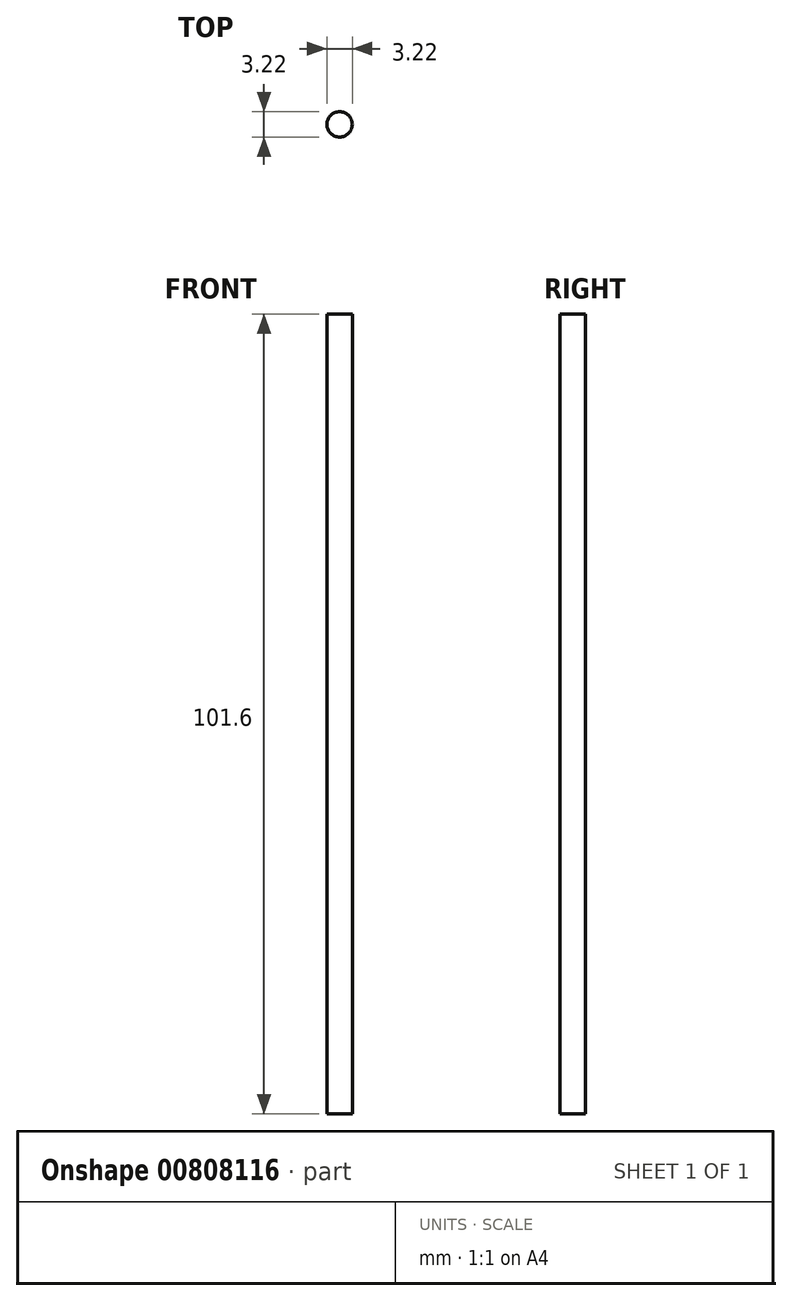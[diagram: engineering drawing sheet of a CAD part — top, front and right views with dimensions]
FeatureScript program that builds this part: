
annotation { "Feature Type Name" : "Feature", "Feature Type Description" : "" }
export const myFeature = defineFeature(function(context is Context, id is Id, definition is map)
    precondition{}
    {
        {
            var Q0;
            Q0=qCreatedBy(makeId("Top.planeOp"),FACE);
            var sketch = newSketch(context, id + "F0", { "sketchPlane" : qUnion([Q0])});
            skCircle(sketch, "E0", {"center": v(0, 0) * mm, "radius": 1.61 * mm});
            skSolve(sketch);
        }
        {
            var Q0;
            Q0=qSketchRegion(id+"F0",true);
            extrude(context, id + "F1", {"entities" : qUnion([Q0]), "depth" : 101.6 * mm, "offsetDistance" : 25.4 * mm});
        }
    });
